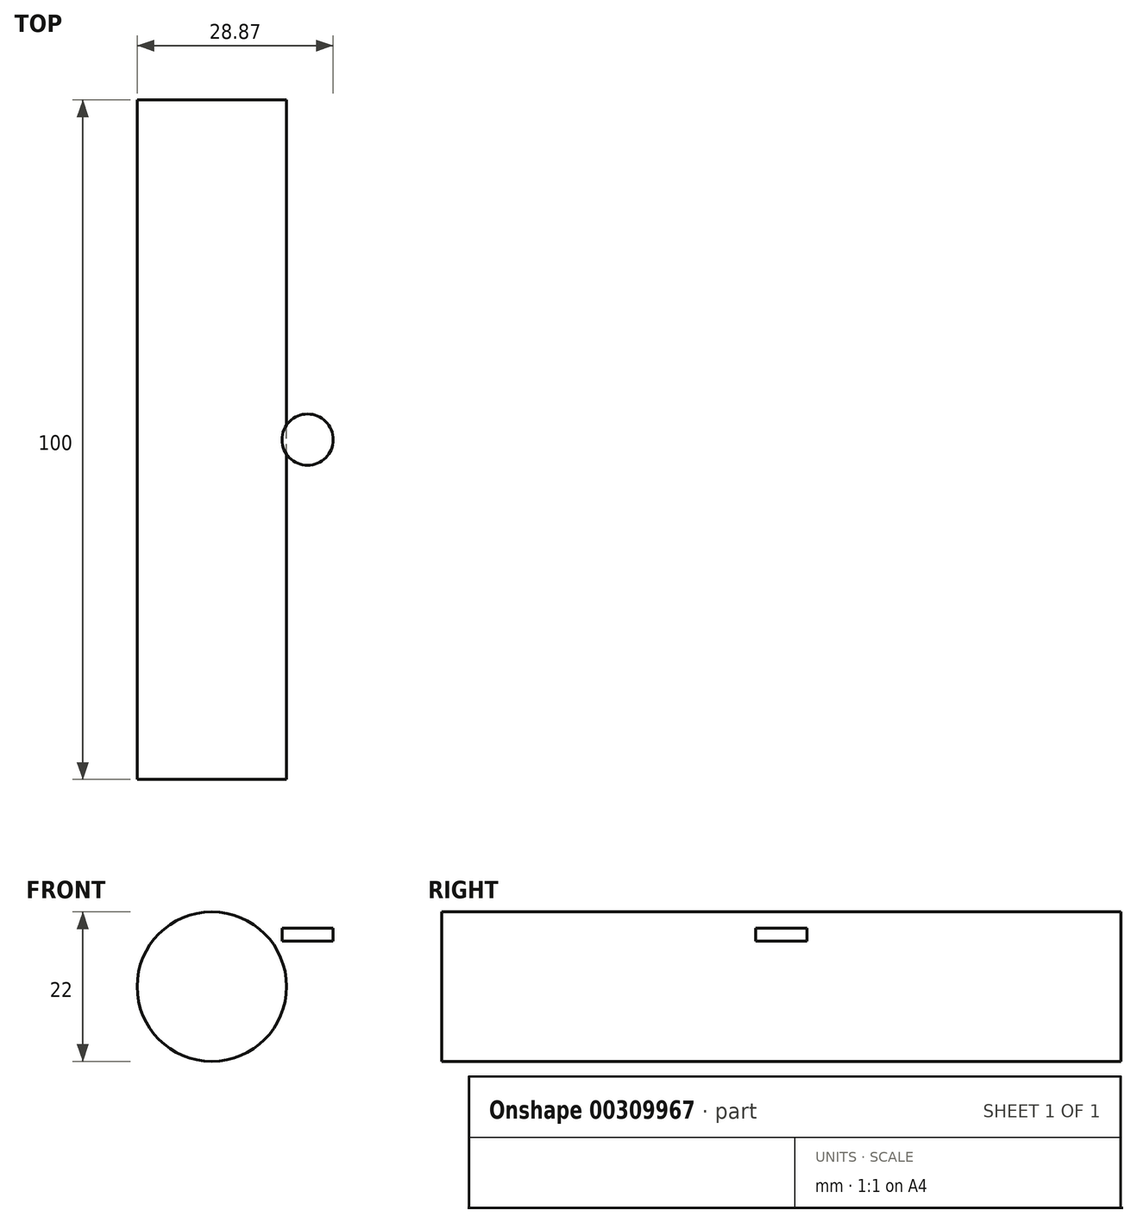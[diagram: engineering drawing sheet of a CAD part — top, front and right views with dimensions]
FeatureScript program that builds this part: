
annotation { "Feature Type Name" : "Feature", "Feature Type Description" : "" }
export const myFeature = defineFeature(function(context is Context, id is Id, definition is map)
    precondition{}
    {
        {
            var Q0;
            Q0=qCreatedBy(makeId("Front.planeOp"),FACE);
            var sketch = newSketch(context, id + "F0", { "sketchPlane" : qUnion([Q0])});
            skCircle(sketch, "E0", {"center": v(-14.1, 0) * mm, "radius": 11 * mm});
            skLineSegment(sketch, "E1", {"start": v(0, 11.34) * mm, "end": v(0, -20.33) * mm});
            skLineSegment(sketch, "E2", {"start": v(-7.25, 8.6) * mm, "end": v(0, 8.6) * mm});
            skLineSegment(sketch, "E3", {"start": v(-7.25, -8.6) * mm, "end": v(0, -8.6) * mm});
            skLineSegment(sketch, "E4.bottom", {"start": v(-1.19, 8.6) * mm, "end": v(0, 8.6) * mm});
            skLineSegment(sketch, "E4.top", {"start": v(-1.19, -8.6) * mm, "end": v(0, -8.6) * mm});
            skLineSegment(sketch, "E4.left", {"start": v(-1.19, 8.6) * mm, "end": v(-1.19, -8.6) * mm});
            skLineSegment(sketch, "E4.right", {"start": v(0, 8.6) * mm, "end": v(0, -8.6) * mm});
            skLineSegment(sketch, "E5.bottom", {"start": v(-3.77, 8.6) * mm, "end": v(0, 8.6) * mm});
            skLineSegment(sketch, "E5.top", {"start": v(-3.77, 6.7) * mm, "end": v(0, 6.7) * mm});
            skLineSegment(sketch, "E5.left", {"start": v(-3.77, 8.6) * mm, "end": v(-3.77, 6.7) * mm});
            skLineSegment(sketch, "E5.right", {"start": v(0, 8.6) * mm, "end": v(0, 6.7) * mm});
            skLineSegment(sketch, "E6.bottom", {"start": v(-7.25, 8.6) * mm, "end": v(-1.19, 8.6) * mm});
            skLineSegment(sketch, "E6.top", {"start": v(-7.25, 10.83) * mm, "end": v(-1.19, 10.83) * mm});
            skLineSegment(sketch, "E6.left", {"start": v(-7.25, 8.6) * mm, "end": v(-7.25, 10.83) * mm});
            skLineSegment(sketch, "E6.right", {"start": v(-1.19, 8.6) * mm, "end": v(-1.19, 10.83) * mm});
            skLineSegment(sketch, "E7.bottom", {"start": v(-7.25, -8.6) * mm, "end": v(-1.19, -8.6) * mm});
            skLineSegment(sketch, "E7.top", {"start": v(-7.25, -11.25) * mm, "end": v(-1.19, -11.25) * mm});
            skLineSegment(sketch, "E7.left", {"start": v(-7.25, -8.6) * mm, "end": v(-7.25, -11.25) * mm});
            skLineSegment(sketch, "E7.right", {"start": v(-1.19, -8.6) * mm, "end": v(-1.19, -11.25) * mm});
            skSolve(sketch);
        }
        {
            var Q0;
            {var subQ0=sQuery(id+"F0.wireOp",EDGE,"E0");var subQ1=makeQuery(id+"F0.imprint","INTERSECT",VERTEX,{"derivedFrom":[subQ0,sQuery(id+"F0.wireOp",EDGE,"E2")]});Q0=makeQuery(id+"F0.imprint","IMPRINT",FACE,{"disambiguationData":[TD([[makeQuery(id+"F0.imprint","IMPRINT",EDGE,{"disambiguationData":[TD([[subQ1,-1.0]])],"derivedFrom":subQ0}),1.0]])]});}
            extrude(context, id + "F1", {"entities" : qUnion([Q0]), "endBound" : BoundingType.SYMMETRIC, "depth" : 100 * mm});
        }
        {
            var Q0;
            {var subQ1=sQuery(id+"F0.wireOp",EDGE,"E2");Q0=makeQuery(id+"F0.imprint","IMPRINT",FACE,{"disambiguationData":[TD([[makeQuery(id+"F0.imprint","IMPRINT",EDGE,{"derivedFrom":subQ1}),-1.0]])]});}
            var Q1;
            Q1=sQuery(id+"F0.wireOp",EDGE,"E4.right");
            revolve(context, id + "F2", {"operationType" : NewBodyOperationType.ADD, "entities" : qUnion([Q0]), "axis" : qUnion([Q1]), "revolveType" : RevolveType.FULL});
        }
    });
